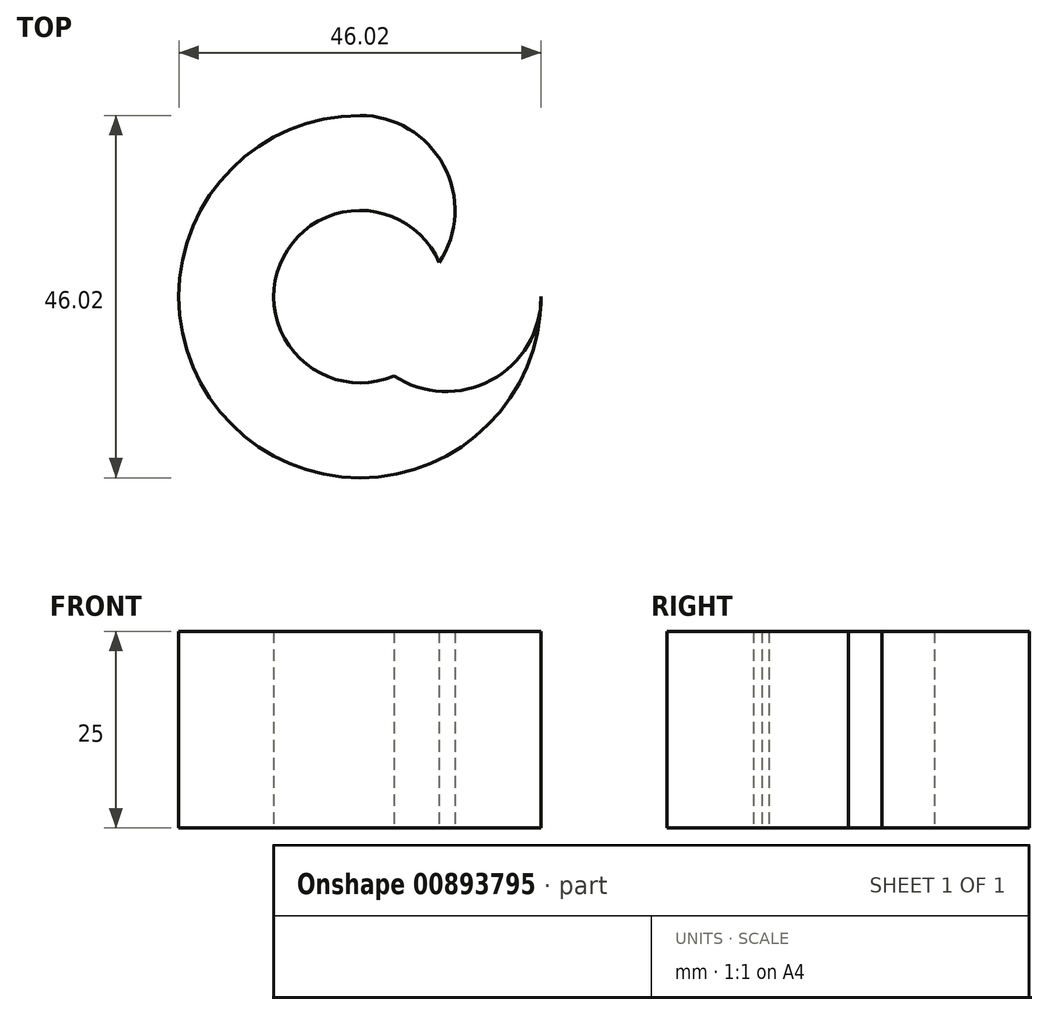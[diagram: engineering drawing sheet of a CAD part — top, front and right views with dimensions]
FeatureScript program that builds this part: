
annotation { "Feature Type Name" : "Feature", "Feature Type Description" : "" }
export const myFeature = defineFeature(function(context is Context, id is Id, definition is map)
    precondition{}
    {
        {
            var Q0;
            Q0=qCreatedBy(makeId("Top.planeOp"),FACE);
            var sketch = newSketch(context, id + "F0", { "sketchPlane" : qUnion([Q0])});
            skCircle(sketch, "E0", {"center": v(0, 0) * mm, "radius": 10.95 * mm});
            skCircle(sketch, "E1", {"center": v(0, 0) * mm, "radius": 23.01 * mm});
            skLineSegment(sketch, "E2.3", {"start": v(8.92, 6.4) * mm, "end": v(8.88, 6.4) * mm});
            skPoint(sketch, "E3.orphan", {"position": v(-13.58, 14.47) * mm});
            skPoint(sketch, "E2.cCircle.center.orphan", {"position": v(0, 16.93) * mm});
            skArc(sketch, "E4.trimOffspring", {"start": v(8.9, 6.38) * mm, "mid": v(8.91, 6.4) * mm, "end": v(8.92, 6.4) * mm, "construction": true});
            skArc(sketch, "E5", {"start": v(0, -23.01) * mm, "mid": v(-10.62, -16.67) * mm, "end": v(-10.07, -4.3) * mm});
            skArc(sketch, "E6", {"start": v(-23.01, 0) * mm, "mid": v(-16.67, 10.62) * mm, "end": v(-4.3, 10.07) * mm});
            skArc(sketch, "E7", {"start": v(0, 23.01) * mm, "mid": v(10.62, 16.67) * mm, "end": v(10.07, 4.3) * mm});
            skArc(sketch, "E8", {"start": v(23.01, 0) * mm, "mid": v(16.67, -10.62) * mm, "end": v(4.3, -10.07) * mm});
            skCircle(sketch, "E9", {"center": v(0, 0) * mm, "radius": 28.19 * mm});
            skSolve(sketch);
        }
        {
            var Q0;
            {var subQ0=sQuery(id+"F0.wireOp",EDGE,"E5");Q0=makeQuery(id+"F0.imprint","IMPRINT",FACE,{"disambiguationData":[TD([[makeQuery(id+"F0.imprint","IMPRINT",EDGE,{"derivedFrom":subQ0}),1.0]])]});}
            var Q1;
            {var subQ0=sQuery(id+"F0.wireOp",EDGE,"E6");Q1=makeQuery(id+"F0.imprint","IMPRINT",FACE,{"disambiguationData":[TD([[makeQuery(id+"F0.imprint","IMPRINT",EDGE,{"derivedFrom":subQ0}),1.0]])]});}
            var Q2;
            {var subQ0=sQuery(id+"F0.wireOp",EDGE,"E5");Q2=makeQuery(id+"F0.imprint","IMPRINT",FACE,{"disambiguationData":[TD([[makeQuery(id+"F0.imprint","IMPRINT",EDGE,{"derivedFrom":subQ0}),-1.0]])]});}
            var Q3;
            {var subQ0=sQuery(id+"F0.wireOp",EDGE,"E7");Q3=makeQuery(id+"F0.imprint","IMPRINT",FACE,{"disambiguationData":[TD([[makeQuery(id+"F0.imprint","IMPRINT",EDGE,{"derivedFrom":subQ0}),1.0]])]});}
            extrude(context, id + "F1", {"entities" : qUnion([Q0, Q1, Q2, Q3]), "depth" : 25 * mm, "offsetDistance" : 25 * mm});
        }
    });
